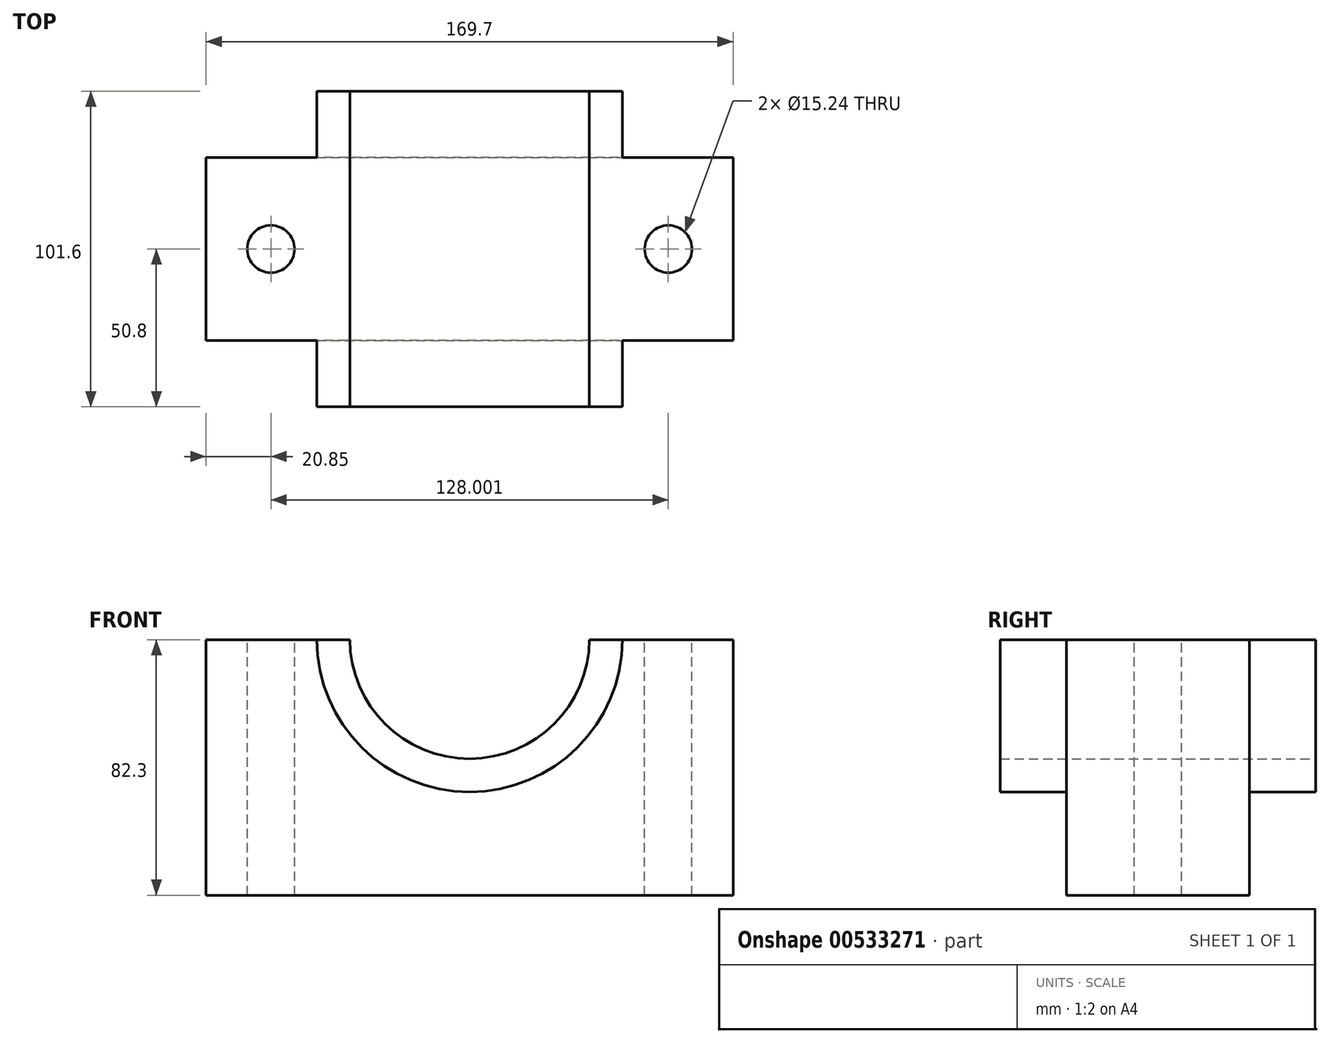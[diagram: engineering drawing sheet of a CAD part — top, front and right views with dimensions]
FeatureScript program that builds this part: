
annotation { "Feature Type Name" : "Feature", "Feature Type Description" : "" }
export const myFeature = defineFeature(function(context is Context, id is Id, definition is map)
    precondition{}
    {
        {
            var Q0;
            Q0=qCreatedBy(makeId("Front.planeOp"),FACE);
            var sketch = newSketch(context, id + "F0", { "sketchPlane" : qUnion([Q0])});
            skLineSegment(sketch, "E0.bottom", {"start": v(84.85, -41.15) * mm, "end": v(-84.85, -41.15) * mm});
            skLineSegment(sketch, "E0.top", {"start": v(84.85, 41.15) * mm, "end": v(49.27, 41.15) * mm});
            skLineSegment(sketch, "E0.left", {"start": v(84.85, -41.15) * mm, "end": v(84.85, 41.15) * mm});
            skLineSegment(sketch, "E0.right", {"start": v(-84.85, -41.15) * mm, "end": v(-84.85, 41.15) * mm});
            skPoint(sketch, "E0.middle", {"position": v(0, 0) * mm});
            skLineSegment(sketch, "E1", {"start": v(-49.27, 41.15) * mm, "end": v(-38.6, 41.15) * mm});
            skLineSegment(sketch, "E2", {"start": v(38.6, 41.15) * mm, "end": v(49.27, 41.15) * mm});
            skArc(sketch, "E3", {"start": v(-49.27, 41.15) * mm, "mid": v(0, -7.87) * mm, "end": v(49.27, 41.15) * mm});
            skArc(sketch, "E4.0", {"start": v(-38.6, 41.2) * mm, "mid": v(0, 2.8) * mm, "end": v(38.6, 41.2) * mm});
            skPoint(sketch, "E5.orphan", {"position": v(0, 41.15) * mm});
            skLineSegment(sketch, "E6.trimOffspring", {"start": v(-38.6, 41.15) * mm, "end": v(-84.85, 41.15) * mm});
            skSolve(sketch);
        }
        {
            var Q0;
            {var subQ0=sQuery(id+"F0.wireOp",EDGE,"E2");Q0=makeQuery(id+"F0.imprint","IMPRINT",FACE,{"disambiguationData":[TD([[makeQuery(id+"F0.imprint","IMPRINT",EDGE,{"derivedFrom":subQ0}),-1.0]])]});}
            extrude(context, id + "F1", {"entities" : qUnion([Q0]), "endBound" : BoundingType.SYMMETRIC, "depth" : 101.6 * mm, "offsetDistance" : 25.4 * mm});
        }
        {
            var Q0;
            Q0 = qSketchRegion(id + "F0", true);
            extrude(context, id + "F2", {"entities" : qUnion([Q0]), "operationType" : NewBodyOperationType.ADD, "endBound" : BoundingType.SYMMETRIC, "depth" : 58.93 * mm, "offsetDistance" : 25.4 * mm});
        }
        {
            var Q0;
            {var subQ0=sQuery(id+"F0.wireOp",EDGE,"E2");Q0=makeQuery(id+"F2.boolean.opBoolean","MERGE",FACE,{"derivedFrom":[makeQuery(id+"F1.opExtrude","SWEPT_FACE",FACE,{"disambiguationData":[OSD([subQ0])]}),makeQuery(id+"F2.opExtrude","SWEPT_FACE",FACE,{"disambiguationData":[OSD([sQuery(id+"F0.wireOp",EDGE,"E0.top"),subQ0])]})]});}
            var sketch = newSketch(context, id + "F3", { "sketchPlane" : qUnion([Q0])});
            skLineSegment(sketch, "E7", {"start": v(38.6, 0) * mm, "end": v(64, 0) * mm});
            skPoint(sketch, "E7.endSnap0", {"position": v(38.6, 0) * mm});
            skSolve(sketch);
        }
        {
            var Q0;
            {var subQ0=sQuery(id+"F0.wireOp",EDGE,"E6.trimOffspring");Q0=makeQuery(id+"F2.boolean.opBoolean","MERGE",FACE,{"derivedFrom":[makeQuery(id+"F1.opExtrude","SWEPT_FACE",FACE,{"disambiguationData":[OSD([subQ0])]}),makeQuery(id+"F2.opExtrude","SWEPT_FACE",FACE,{"disambiguationData":[OSD([subQ0])]})]});}
            var sketch = newSketch(context, id + "F4", { "sketchPlane" : qUnion([Q0])});
            skLineSegment(sketch, "E8", {"start": v(-38.6, 0) * mm, "end": v(-64, 0) * mm});
            skPoint(sketch, "E8.endSnap0", {"position": v(-38.6, 0) * mm});
            skSolve(sketch);
        }
        {
            var Q0;
            Q0=sQuery(id+"F4.wireOp",VERTEX,"E8.end");
            var Q1;
            Q1=makeQuery(id+"F1.opExtrude","SWEPT_BODY",BODY,{"disambiguationData":[OSD([sQuery(id+"F0.wireOp",EDGE,"E2"),sQuery(id+"F0.wireOp",EDGE,"E3"),sQuery(id+"F0.wireOp",EDGE,"E4.0"),sQuery(id+"F0.wireOp",EDGE,"E6.trimOffspring")])]});
            hole(context, id + "F5", {"style" : HoleStyle.SIMPLE, "endStyle" : HoleEndStyle.THROUGH, "holeDiameter" : 15.24 * mm, "isTappedThrough" : true, "tappedDepth" : 12.7 * mm, "tapClearance" : 3, "locations" : qUnion([Q0]), "scope" : qUnion([Q1])});
        }
        {
            var Q0;
            Q0=sQuery(id+"F3.wireOp",VERTEX,"E7.end");
            var Q1;
            Q1=makeQuery(id+"F1.opExtrude","SWEPT_BODY",BODY,{"disambiguationData":[OSD([sQuery(id+"F0.wireOp",EDGE,"E2"),sQuery(id+"F0.wireOp",EDGE,"E3"),sQuery(id+"F0.wireOp",EDGE,"E4.0"),sQuery(id+"F0.wireOp",EDGE,"E6.trimOffspring")])]});
            hole(context, id + "F6", {"style" : HoleStyle.SIMPLE, "endStyle" : HoleEndStyle.THROUGH, "holeDiameter" : 15.24 * mm, "isTappedThrough" : true, "tappedDepth" : 12.7 * mm, "tapClearance" : 3, "locations" : qUnion([Q0]), "scope" : qUnion([Q1])});
        }
    });
